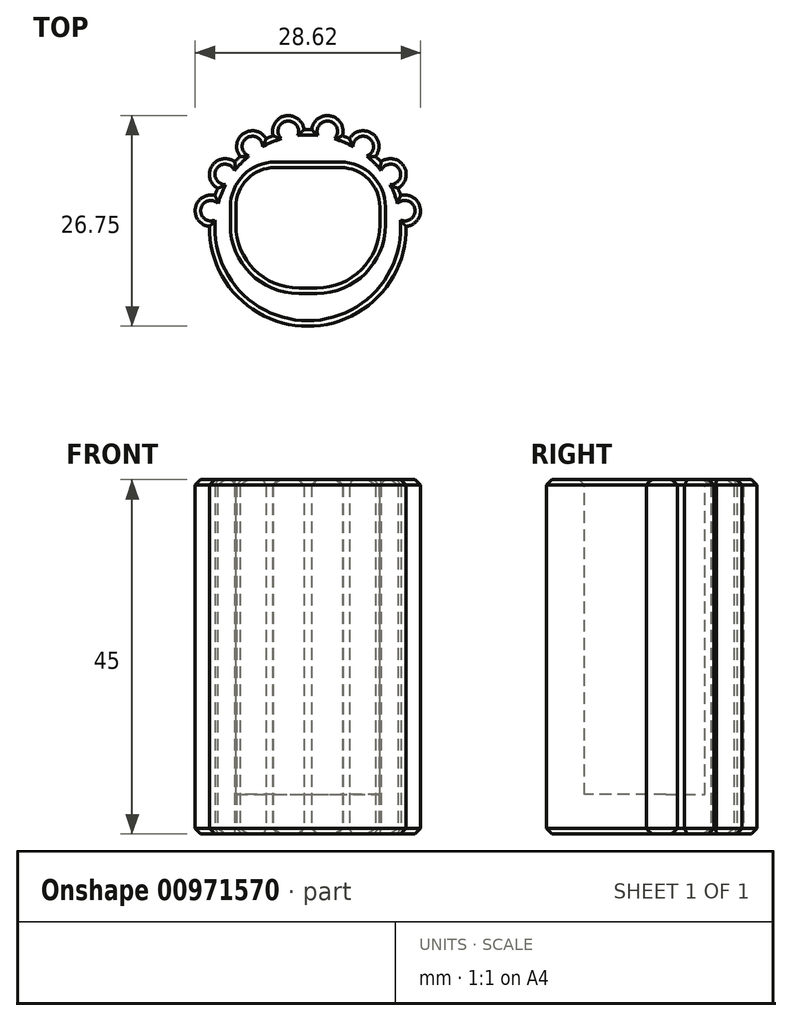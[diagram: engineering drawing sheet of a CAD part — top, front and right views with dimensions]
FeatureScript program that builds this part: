
annotation { "Feature Type Name" : "Feature", "Feature Type Description" : "" }
export const myFeature = defineFeature(function(context is Context, id is Id, definition is map)
    precondition{}
    {
        {
            var Q0;
            Q0=qCreatedBy(makeId("Top.planeOp"),FACE);
            var sketch = newSketch(context, id + "F0", { "sketchPlane" : qUnion([Q0])});
            skCircle(sketch, "E0", {"center": v(0, 0) * mm, "radius": 12.5 * mm});
            skLineSegment(sketch, "E1", {"start": v(0, 0) * mm, "end": v(24.32, 4.29) * mm, "construction": true});
            skArc(sketch, "E2", {"start": v(12.5, 0.18) * mm, "mid": v(14.28, 2.52) * mm, "end": v(11.8, 4.1) * mm});
            skArc(sketch, "E3.1.0", {"start": v(11.45, 5.02) * mm, "mid": v(12.18, 7.87) * mm, "end": v(9.28, 8.37) * mm});
            skArc(sketch, "E3.2.0", {"start": v(8.6, 9.07) * mm, "mid": v(8.17, 11.98) * mm, "end": v(5.3, 11.32) * mm});
            skArc(sketch, "E3.3.0", {"start": v(4.4, 11.7) * mm, "mid": v(2.87, 14.21) * mm, "end": v(0.5, 12.5) * mm});
            skArc(sketch, "E3.4.0", {"start": v(-0.5, 12.5) * mm, "mid": v(-2.87, 14.21) * mm, "end": v(-4.4, 11.7) * mm});
            skArc(sketch, "E3.5.0", {"start": v(-5.3, 11.32) * mm, "mid": v(-8.17, 11.98) * mm, "end": v(-8.6, 9.07) * mm});
            skArc(sketch, "E3.6.0", {"start": v(-9.28, 8.37) * mm, "mid": v(-12.18, 7.87) * mm, "end": v(-11.45, 5.02) * mm});
            skArc(sketch, "E3.7.0", {"start": v(-11.8, 4.1) * mm, "mid": v(-14.28, 2.52) * mm, "end": v(-12.5, 0.18) * mm});
            skLineSegment(sketch, "E3.anchor1", {"start": v(0, 0) * mm, "end": v(12.31, 2.17) * mm, "construction": true});
            skLineSegment(sketch, "E3.anchor2", {"start": v(0, 0) * mm, "end": v(-12.31, 2.17) * mm, "construction": true});
            skSolve(sketch);
        }
        {
            var Q0;
            Q0 = qSketchRegion(id + "F0", true);
            extrude(context, id + "F1", {"entities" : qUnion([Q0]), "depth" : 45 * mm, "offsetDistance" : 25 * mm});
        }
        {
            var Q0;
            Q0=makeQuery(id+"F1.opExtrude","CAP_FACE",FACE,{"disambiguationData":[OSD([sQuery(id+"F0.wireOp",EDGE,"E0"),sQuery(id+"F0.wireOp",EDGE,"zvGOjm8Q-2Iy8-kKSx-GrVq-IIdAKqRGmpF0"),sQuery(id+"F0.wireOp",EDGE,"27b2f94e-c7c3-4ddf-90f0-9bd7903cea88.1.0"),sQuery(id+"F0.wireOp",EDGE,"27b2f94e-c7c3-4ddf-90f0-9bd7903cea88.2.0"),sQuery(id+"F0.wireOp",EDGE,"27b2f94e-c7c3-4ddf-90f0-9bd7903cea88.3.0"),sQuery(id+"F0.wireOp",EDGE,"27b2f94e-c7c3-4ddf-90f0-9bd7903cea88.4.0"),sQuery(id+"F0.wireOp",EDGE,"27b2f94e-c7c3-4ddf-90f0-9bd7903cea88.5.0"),sQuery(id+"F0.wireOp",EDGE,"27b2f94e-c7c3-4ddf-90f0-9bd7903cea88.6.0"),sQuery(id+"F0.wireOp",EDGE,"27b2f94e-c7c3-4ddf-90f0-9bd7903cea88.7.0"),sQuery(id+"F0.wireOp",EDGE,"27b2f94e-c7c3-4ddf-90f0-9bd7903cea88.8.0"),sQuery(id+"F0.wireOp",EDGE,"27b2f94e-c7c3-4ddf-90f0-9bd7903cea88.9.0"),sQuery(id+"F0.wireOp",EDGE,"27b2f94e-c7c3-4ddf-90f0-9bd7903cea88.10.0"),sQuery(id+"F0.wireOp",EDGE,"27b2f94e-c7c3-4ddf-90f0-9bd7903cea88.11.0"),sQuery(id+"F0.wireOp",EDGE,"27b2f94e-c7c3-4ddf-90f0-9bd7903cea88.12.0"),sQuery(id+"F0.wireOp",EDGE,"27b2f94e-c7c3-4ddf-90f0-9bd7903cea88.13.0"),sQuery(id+"F0.wireOp",EDGE,"27b2f94e-c7c3-4ddf-90f0-9bd7903cea88.14.0"),sQuery(id+"F0.wireOp",EDGE,"27b2f94e-c7c3-4ddf-90f0-9bd7903cea88.15.0"),sQuery(id+"F0.wireOp",EDGE,"27b2f94e-c7c3-4ddf-90f0-9bd7903cea88.16.0"),sQuery(id+"F0.wireOp",EDGE,"27b2f94e-c7c3-4ddf-90f0-9bd7903cea88.17.0"),sQuery(id+"F0.wireOp",EDGE,"27b2f94e-c7c3-4ddf-90f0-9bd7903cea88.18.0"),sQuery(id+"F0.wireOp",EDGE,"27b2f94e-c7c3-4ddf-90f0-9bd7903cea88.19.0")])],"isStart":false});
            var sketch = newSketch(context, id + "F2", { "sketchPlane" : qUnion([Q0])});
            skLineSegment(sketch, "E4.bottom", {"start": v(-4.15, 7.65) * mm, "end": v(4.15, 7.65) * mm});
            skLineSegment(sketch, "E4.top", {"start": v(-1.15, -7.65) * mm, "end": v(1.15, -7.65) * mm});
            skLineSegment(sketch, "E4.left", {"start": v(-9.15, 2.65) * mm, "end": v(-9.15, 0.35) * mm});
            skLineSegment(sketch, "E4.right", {"start": v(9.15, 2.65) * mm, "end": v(9.15, 0.35) * mm});
            skLineSegment(sketch, "E5", {"start": v(-9.15, -7.65) * mm, "end": v(9.15, 7.65) * mm, "construction": true});
            skPoint(sketch, "E6.visualSharp", {"position": v(-9.15, 7.65) * mm});
            skArc(sketch, "E6.filletArc", {"start": v(-4.15, 7.65) * mm, "mid": v(-7.69, 6.19) * mm, "end": v(-9.15, 2.65) * mm});
            skPoint(sketch, "E7.visualSharp", {"position": v(9.15, 7.65) * mm});
            skArc(sketch, "E7.filletArc", {"start": v(9.15, 2.65) * mm, "mid": v(7.69, 6.19) * mm, "end": v(4.15, 7.65) * mm});
            skPoint(sketch, "E8.visualSharp", {"position": v(9.15, -7.65) * mm});
            skArc(sketch, "E8.filletArc", {"start": v(1.15, -7.65) * mm, "mid": v(6.8, -5.3) * mm, "end": v(9.15, 0.35) * mm});
            skPoint(sketch, "E9.visualSharp", {"position": v(-9.15, -7.65) * mm});
            skArc(sketch, "E9.filletArc", {"start": v(-9.15, 0.35) * mm, "mid": v(-6.8, -5.3) * mm, "end": v(-1.15, -7.65) * mm});
            skSolve(sketch);
        }
        {
            var Q0;
            Q0 = qSketchRegion(id + "F2", true);
            extrude(context, id + "F3", {"entities" : qUnion([Q0]), "operationType" : NewBodyOperationType.REMOVE, "oppositeDirection" : true, "depth" : 40 * mm, "offsetDistance" : 25 * mm});
        }
        {
            var Q0;
            Q0=makeQuery(id+"F1.opExtrude","CAP_FACE",FACE,{"disambiguationData":[OSD([sQuery(id+"F0.wireOp",EDGE,"E0"),sQuery(id+"F0.wireOp",EDGE,"zvGOjm8Q-2Iy8-kKSx-GrVq-IIdAKqRGmpF0"),sQuery(id+"F0.wireOp",EDGE,"27b2f94e-c7c3-4ddf-90f0-9bd7903cea88.1.0"),sQuery(id+"F0.wireOp",EDGE,"27b2f94e-c7c3-4ddf-90f0-9bd7903cea88.2.0"),sQuery(id+"F0.wireOp",EDGE,"27b2f94e-c7c3-4ddf-90f0-9bd7903cea88.3.0"),sQuery(id+"F0.wireOp",EDGE,"27b2f94e-c7c3-4ddf-90f0-9bd7903cea88.4.0"),sQuery(id+"F0.wireOp",EDGE,"27b2f94e-c7c3-4ddf-90f0-9bd7903cea88.5.0"),sQuery(id+"F0.wireOp",EDGE,"27b2f94e-c7c3-4ddf-90f0-9bd7903cea88.6.0"),sQuery(id+"F0.wireOp",EDGE,"27b2f94e-c7c3-4ddf-90f0-9bd7903cea88.7.0"),sQuery(id+"F0.wireOp",EDGE,"27b2f94e-c7c3-4ddf-90f0-9bd7903cea88.8.0"),sQuery(id+"F0.wireOp",EDGE,"27b2f94e-c7c3-4ddf-90f0-9bd7903cea88.9.0"),sQuery(id+"F0.wireOp",EDGE,"27b2f94e-c7c3-4ddf-90f0-9bd7903cea88.10.0"),sQuery(id+"F0.wireOp",EDGE,"27b2f94e-c7c3-4ddf-90f0-9bd7903cea88.11.0"),sQuery(id+"F0.wireOp",EDGE,"27b2f94e-c7c3-4ddf-90f0-9bd7903cea88.12.0"),sQuery(id+"F0.wireOp",EDGE,"27b2f94e-c7c3-4ddf-90f0-9bd7903cea88.13.0"),sQuery(id+"F0.wireOp",EDGE,"27b2f94e-c7c3-4ddf-90f0-9bd7903cea88.14.0"),sQuery(id+"F0.wireOp",EDGE,"27b2f94e-c7c3-4ddf-90f0-9bd7903cea88.15.0"),sQuery(id+"F0.wireOp",EDGE,"27b2f94e-c7c3-4ddf-90f0-9bd7903cea88.16.0"),sQuery(id+"F0.wireOp",EDGE,"27b2f94e-c7c3-4ddf-90f0-9bd7903cea88.17.0"),sQuery(id+"F0.wireOp",EDGE,"27b2f94e-c7c3-4ddf-90f0-9bd7903cea88.18.0"),sQuery(id+"F0.wireOp",EDGE,"27b2f94e-c7c3-4ddf-90f0-9bd7903cea88.19.0")])],"isStart":true});
            var Q1;
            Q1=makeQuery(id+"F1.opExtrude","CAP_FACE",FACE,{"disambiguationData":[OSD([sQuery(id+"F0.wireOp",EDGE,"E0"),sQuery(id+"F0.wireOp",EDGE,"zvGOjm8Q-2Iy8-kKSx-GrVq-IIdAKqRGmpF0"),sQuery(id+"F0.wireOp",EDGE,"27b2f94e-c7c3-4ddf-90f0-9bd7903cea88.1.0"),sQuery(id+"F0.wireOp",EDGE,"27b2f94e-c7c3-4ddf-90f0-9bd7903cea88.2.0"),sQuery(id+"F0.wireOp",EDGE,"27b2f94e-c7c3-4ddf-90f0-9bd7903cea88.3.0"),sQuery(id+"F0.wireOp",EDGE,"27b2f94e-c7c3-4ddf-90f0-9bd7903cea88.4.0"),sQuery(id+"F0.wireOp",EDGE,"27b2f94e-c7c3-4ddf-90f0-9bd7903cea88.5.0"),sQuery(id+"F0.wireOp",EDGE,"27b2f94e-c7c3-4ddf-90f0-9bd7903cea88.6.0"),sQuery(id+"F0.wireOp",EDGE,"27b2f94e-c7c3-4ddf-90f0-9bd7903cea88.7.0"),sQuery(id+"F0.wireOp",EDGE,"27b2f94e-c7c3-4ddf-90f0-9bd7903cea88.8.0"),sQuery(id+"F0.wireOp",EDGE,"27b2f94e-c7c3-4ddf-90f0-9bd7903cea88.9.0"),sQuery(id+"F0.wireOp",EDGE,"27b2f94e-c7c3-4ddf-90f0-9bd7903cea88.10.0"),sQuery(id+"F0.wireOp",EDGE,"27b2f94e-c7c3-4ddf-90f0-9bd7903cea88.11.0"),sQuery(id+"F0.wireOp",EDGE,"27b2f94e-c7c3-4ddf-90f0-9bd7903cea88.12.0"),sQuery(id+"F0.wireOp",EDGE,"27b2f94e-c7c3-4ddf-90f0-9bd7903cea88.13.0"),sQuery(id+"F0.wireOp",EDGE,"27b2f94e-c7c3-4ddf-90f0-9bd7903cea88.14.0"),sQuery(id+"F0.wireOp",EDGE,"27b2f94e-c7c3-4ddf-90f0-9bd7903cea88.15.0"),sQuery(id+"F0.wireOp",EDGE,"27b2f94e-c7c3-4ddf-90f0-9bd7903cea88.16.0"),sQuery(id+"F0.wireOp",EDGE,"27b2f94e-c7c3-4ddf-90f0-9bd7903cea88.17.0"),sQuery(id+"F0.wireOp",EDGE,"27b2f94e-c7c3-4ddf-90f0-9bd7903cea88.18.0"),sQuery(id+"F0.wireOp",EDGE,"27b2f94e-c7c3-4ddf-90f0-9bd7903cea88.19.0")])],"isStart":false});
            chamfer(context, id + "F4", {"entities" : qUnion([Q0, Q1]), "width" : .7 * mm, "tangentPropagation" : true});
        }
    });
